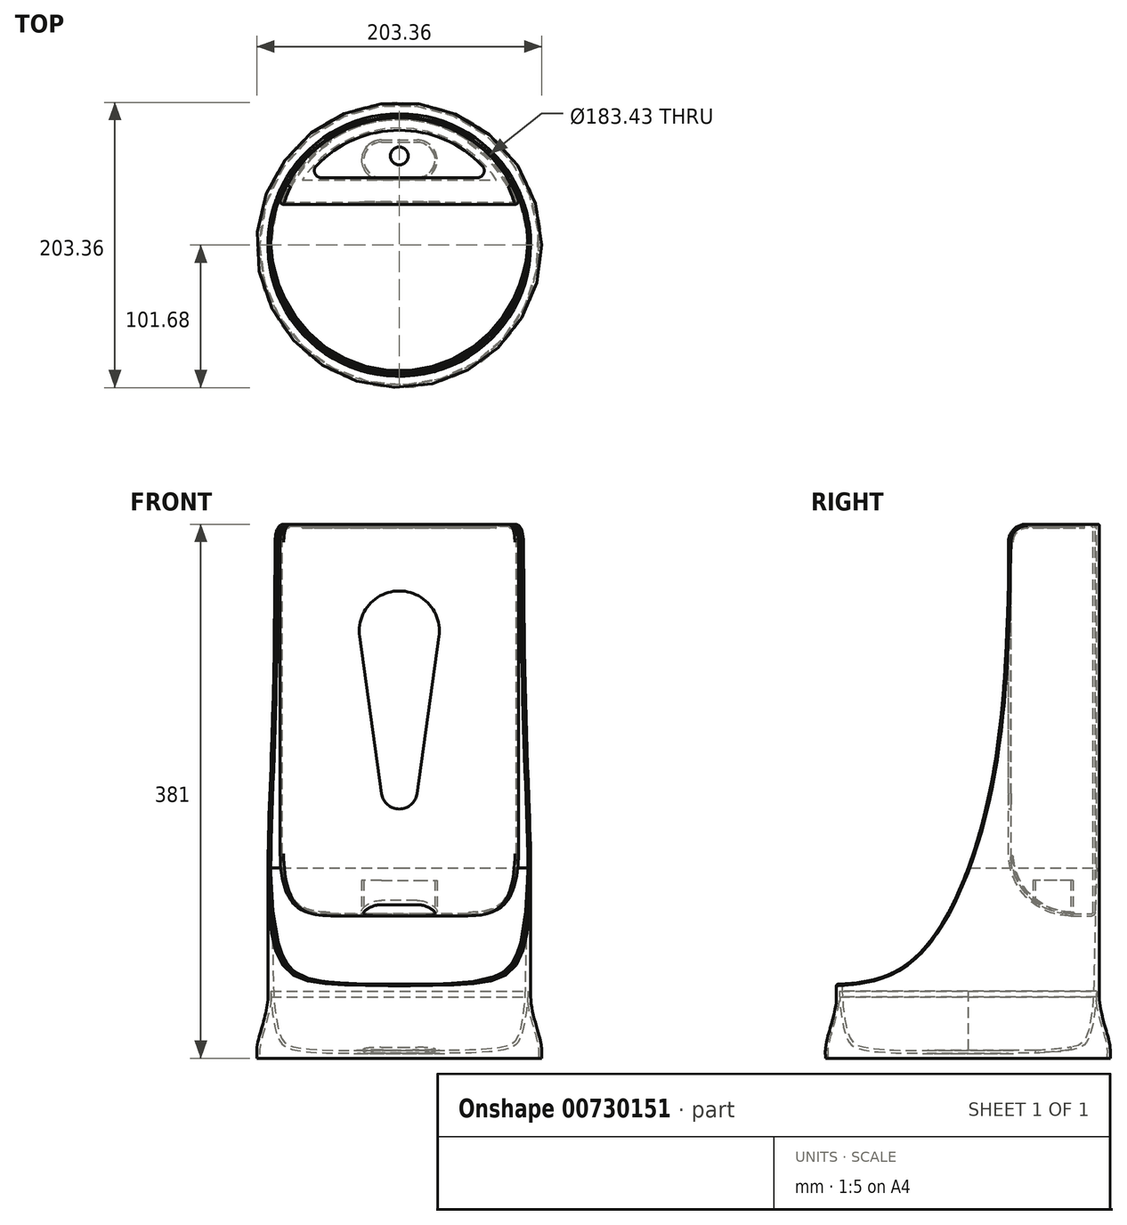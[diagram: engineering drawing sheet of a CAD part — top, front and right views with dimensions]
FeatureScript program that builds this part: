
annotation { "Feature Type Name" : "Feature", "Feature Type Description" : "" }
export const myFeature = defineFeature(function(context is Context, id is Id, definition is map)
    precondition{}
    {
        {
            var Q0;
            Q0=qCreatedBy(makeId("Right.planeOp"),FACE);
            var sketch = newSketch(context, id + "F0", { "sketchPlane" : qUnion([Q0])});
            skLineSegment(sketch, "E0", {"start": v(0, 343.86) * mm, "end": v(0, -187.02) * mm, "construction": true});
            skLineSegment(sketch, "E1", {"start": v(0, 381) * mm, "end": v(0, 0) * mm});
            skLineSegment(sketch, "E2", {"start": v(0, 0) * mm, "end": v(101.6, 0) * mm});
            skLineSegment(sketch, "E3", {"start": v(93.75, 381) * mm, "end": v(0, 381) * mm});
            skLineSegment(sketch, "E4", {"start": v(93.75, 381) * mm, "end": v(93.75, 43.78) * mm});
            skFitSpline(sketch, "E5", {"points": [v(93.75, 43.78) * mm, v(99.9, 15.52) * mm, v(101.6, 6.52) * mm, v(101.6, 0) * mm], "startDerivative": vector(0, -53.97) * mm, "endDerivative": vector(-0.88, -40.06) * mm});
            skSolve(sketch);
        }
        {
            var Q0;
            Q0=makeQuery(id+"F0.imprint","IMPRINT",FACE,{"disambiguationData":[TD([[makeQuery(id+"F0.imprint","IMPRINT",EDGE,{"derivedFrom":sQuery(id+"F0.wireOp",EDGE,"E1")}),1.0]])]});
            var Q1;
            Q1=sQuery(id+"F0.wireOp",EDGE,"E0");
            revolve(context, id + "F1", {"surfaceOperationType" : NewSurfaceOperationType.NEW, "entities" : qUnion([Q0]), "axis" : qUnion([Q1]), "revolveType" : RevolveType.FULL});
        }
        {
            var Q0;
            Q0=qCreatedBy(makeId("Right.planeOp"),FACE);
            var sketch = newSketch(context, id + "F2", { "sketchPlane" : qUnion([Q0])});
            skFitSpline(sketch, "E6.0", {"points": [v(93.75, 43.78) * mm, v(93.75, 34.95) * mm, v(100.28, 16.1) * mm, v(101.8, 6.5) * mm, v(101.67, 3.11) * mm, v(101.6, 0) * mm], "construction": true});
            skLineSegment(sketch, "E7.0", {"start": v(93.75, 381) * mm, "end": v(93.75, 43.78) * mm, "construction": true});
            skFitSpline(sketch, "E8.0", {"points": [v(91.72, 43.78) * mm, v(91.72, 41.36) * mm, v(92.29, 36.24) * mm, v(93.83, 29.57) * mm, v(95.23, 24.44) * mm, v(96.29, 20.8) * mm, v(97.1, 18) * mm, v(97.68, 15.97) * mm, v(98.06, 14.57) * mm, v(98.4, 13.29) * mm, v(98.77, 11.72) * mm, v(99.12, 10) * mm, v(99.4, 8.25) * mm, v(99.53, 7) * mm, v(99.6, 6.06) * mm, v(99.64, 5.16) * mm, v(99.65, 4) * mm, v(99.62, 2.33) * mm, v(99.59, 0.88) * mm, v(99.57, 0.04) * mm]});
            skLineSegment(sketch, "E8.1", {"start": v(91.72, 304.8) * mm, "end": v(91.72, 43.78) * mm, "construction": true});
            skLineSegment(sketch, "E9", {"start": v(91.72, 43.78) * mm, "end": v(91.72, 47.88) * mm});
            skFitSpline(sketch, "E10", {"points": [v(91.72, 47.88) * mm, v(86.67, 15.25) * mm, v(74.28, 5.84) * mm, v(29.74, 3.52) * mm], "startDerivative": vector(-1.81, -78.5) * mm, "endDerivative": vector(-58.98, 0) * mm});
            skLineSegment(sketch, "E11", {"start": v(29.74, 3.52) * mm, "end": v(0, 3.52) * mm});
            skLineSegment(sketch, "E12", {"start": v(0, 3.52) * mm, "end": v(0, -5.27) * mm});
            skLineSegment(sketch, "E13", {"start": v(0, -5.27) * mm, "end": v(98.97, -5.27) * mm});
            skLineSegment(sketch, "E14", {"start": v(98.97, -5.27) * mm, "end": v(99.57, 0.04) * mm});
            skSolve(sketch);
        }
        {
            var Q0;
            Q0 = qSketchRegion(id + "F2", true);
            var Q1;
            Q1=sQuery(id+"F0.wireOp",EDGE,"E0");
            revolve(context, id + "F3", {"operationType" : NewBodyOperationType.REMOVE, "surfaceOperationType" : NewSurfaceOperationType.NEW, "entities" : qUnion([Q0]), "axis" : qUnion([Q1]), "revolveType" : RevolveType.FULL, "oppositeDirection" : true});
        }
        {
            var Q0;
            Q0=makeQuery(id+"F1.opRevolve","SWEPT_FACE",FACE,{"disambiguationData":[OSD([sQuery(id+"F0.wireOp",EDGE,"E3")])]});
            shell(context, id + "F4", {"entities" : qUnion([Q0]), "thickness" : 2.03 * mm});
        }
        {
            var Q0;
            Q0=qCreatedBy(makeId("Right.planeOp"),FACE);
            var sketch = newSketch(context, id + "F5", { "sketchPlane" : qUnion([Q0])});
            skFitSpline(sketch, "E15", {"points": [v(29.87, 383.03) * mm, v(18.53, 206.1) * mm, v(-39.75, 69.98) * mm, v(-93.97, 52.7) * mm, v(-140.33, 52.7) * mm], "startDerivative": vector(-12.72, -336.18) * mm, "endDerivative": vector(-243.15, 2.79) * mm});
            skLineSegment(sketch, "E16", {"start": v(29.87, 383.03) * mm, "end": v(-142.32, 383.03) * mm});
            skLineSegment(sketch, "E17", {"start": v(-142.32, 383.03) * mm, "end": v(-140.33, 52.7) * mm});
            skSolve(sketch);
        }
        {
            var Q0;
            Q0=makeQuery(id+"F5.imprint","IMPRINT",FACE,{"disambiguationData":[TD([[makeQuery(id+"F5.imprint","IMPRINT",EDGE,{"derivedFrom":sQuery(id+"F5.wireOp",EDGE,"E15")}),-1.0]])]});
            extrude(context, id + "F6", {"entities" : qUnion([Q0]), "operationType" : NewBodyOperationType.REMOVE, "endBound" : BoundingType.THROUGH_ALL, "oppositeDirection" : true, "depth" : 25.4 * mm, "offsetDistance" : 25.4 * mm, "hasSecondDirection" : true, "secondDirectionBound" : BoundingType.THROUGH_ALL, "secondDirectionOppositeDirection" : false, "secondDirectionDepth" : 25.4 * mm});
        }
        {
            var Q0;
            Q0=makeQuery(id+"F6.boolean.opBoolean","INTERSECT",EDGE,{"disambiguationData":[OD(0.0)],"derivedFrom":[makeQuery(id+"F1.opRevolve","SWEPT_FACE",FACE,{"disambiguationData":[OSD([sQuery(id+"F0.wireOp",EDGE,"E3")])]}),makeQuery(id+"F6.opExtrude","SWEPT_FACE",FACE,{"disambiguationData":[OSD([sQuery(id+"F5.wireOp",EDGE,"E15")])]})]});
            var Q1;
            Q1=makeQuery(id+"F6.boolean.opBoolean","INTERSECT",EDGE,{"disambiguationData":[OD(1.0)],"derivedFrom":[makeQuery(id+"F1.opRevolve","SWEPT_FACE",FACE,{"disambiguationData":[OSD([sQuery(id+"F0.wireOp",EDGE,"E3")])]}),makeQuery(id+"F6.opExtrude","SWEPT_FACE",FACE,{"disambiguationData":[OSD([sQuery(id+"F5.wireOp",EDGE,"E15")])]})]});
            fillet(context, id + "F7", {"entities" : qUnion([Q0, Q1]), "radius" : 12.7 * mm, "tangentPropagation" : true, "allowEdgeOverflow" : false});
        }
        {
            var Q0;
            Q0=makeQuery(id+"F7.opFillet","BLEND_EDGE",EDGE,{"blendedFrom":[makeQuery(id+"F6.boolean.opBoolean","INTERSECT",EDGE,{"disambiguationData":[OD(0.0)],"derivedFrom":[makeQuery(id+"F1.opRevolve","SWEPT_FACE",FACE,{"disambiguationData":[OSD([sQuery(id+"F0.wireOp",EDGE,"E3")])]}),makeQuery(id+"F6.opExtrude","SWEPT_FACE",FACE,{"disambiguationData":[OSD([sQuery(id+"F5.wireOp",EDGE,"E15")])]})]}),makeQuery(id+"F4.opShell","OFFSET_FACE",FACE,{"disambiguationData":[OSD([sQuery(id+"F0.wireOp",EDGE,"E4")])]})],"blendedInto":[makeQuery(id+"F4.opShell","OFFSET_FACE",FACE,{"disambiguationData":[OSD([sQuery(id+"F0.wireOp",EDGE,"E4")])]})]});
            var Q1;
            Q1=makeQuery(id+"F7.opFillet","BLEND_EDGE",EDGE,{"blendedFrom":[makeQuery(id+"F6.boolean.opBoolean","INTERSECT",EDGE,{"disambiguationData":[OD(0.0)],"derivedFrom":[makeQuery(id+"F1.opRevolve","SWEPT_FACE",FACE,{"disambiguationData":[OSD([sQuery(id+"F0.wireOp",EDGE,"E3")])]}),makeQuery(id+"F6.opExtrude","SWEPT_FACE",FACE,{"disambiguationData":[OSD([sQuery(id+"F5.wireOp",EDGE,"E15")])]})]}),makeQuery(id+"F1.opRevolve","SWEPT_FACE",FACE,{"disambiguationData":[OSD([sQuery(id+"F0.wireOp",EDGE,"E4")])]})],"blendedInto":[makeQuery(id+"F1.opRevolve","SWEPT_FACE",FACE,{"disambiguationData":[OSD([sQuery(id+"F0.wireOp",EDGE,"E4")])]})]});
            var Q2;
            Q2=makeQuery(id+"F6.boolean.opBoolean","INTERSECT",EDGE,{"disambiguationData":[OD(0.0)],"derivedFrom":[makeQuery(id+"F4.opShell","OFFSET_FACE",FACE,{"disambiguationData":[OSD([sQuery(id+"F0.wireOp",EDGE,"E4")])]}),makeQuery(id+"F6.opExtrude","SWEPT_FACE",FACE,{"disambiguationData":[OSD([sQuery(id+"F5.wireOp",EDGE,"E15")])]})]});
            var Q3;
            Q3=makeQuery(id+"F6.boolean.opBoolean","INTERSECT",EDGE,{"derivedFrom":[makeQuery(id+"F4.opShell","OFFSET_FACE",FACE,{"disambiguationData":[OSD([sQuery(id+"F2.wireOp",EDGE,"E10")])]}),makeQuery(id+"F6.opExtrude","SWEPT_FACE",FACE,{"disambiguationData":[OSD([sQuery(id+"F5.wireOp",EDGE,"E15")])]})]});
            fillet(context, id + "F8", {"entities" : qUnion([Q0, Q1, Q2, Q3]), "radius" : 1.02 * mm, "tangentPropagation" : true, "allowEdgeOverflow" : false});
        }
        {
            var Q0;
            Q0=qCreatedBy(makeId("Top.planeOp"),FACE);
            var Q1;
            {var subQ0=sQuery(id+"F0.wireOp",EDGE,"E4");var subQ1=sQuery(id+"F0.wireOp",EDGE,"E3");var subQ2=makeQuery(id+"F6.boolean.opBoolean","INTERSECT",EDGE,{"disambiguationData":[OD(1.0)],"derivedFrom":[makeQuery(id+"F1.opRevolve","SWEPT_FACE",FACE,{"disambiguationData":[OSD([subQ1])]}),makeQuery(id+"F6.opExtrude","SWEPT_FACE",FACE,{"disambiguationData":[OSD([sQuery(id+"F5.wireOp",EDGE,"E15")])]})]});Q1=makeQuery(id+"F8.opFillet","BLEND_VERTEX",VERTEX,{"blendedFrom":[makeQuery(id+"F1.opRevolve","SWEPT_EDGE",EDGE,{"disambiguationData":[OSD([subQ1,subQ0])]}),makeQuery(id+"F4.opShell","OFFSET_EDGE",EDGE,{"disambiguationData":[OSD([subQ1,subQ0])]}),makeQuery(id+"F7.opFillet","BLEND_EDGE",EDGE,{"blendedFrom":[subQ2,makeQuery(id+"F1.opRevolve","SWEPT_FACE",FACE,{"disambiguationData":[OSD([subQ0])]})],"blendedInto":[makeQuery(id+"F1.opRevolve","SWEPT_FACE",FACE,{"disambiguationData":[OSD([subQ0])]})]}),makeQuery(id+"F7.opFillet","BLEND_EDGE",EDGE,{"blendedFrom":[subQ2,makeQuery(id+"F4.opShell","OFFSET_FACE",FACE,{"disambiguationData":[OSD([subQ0])]})],"blendedInto":[makeQuery(id+"F4.opShell","OFFSET_FACE",FACE,{"disambiguationData":[OSD([subQ0])]})]})],"blendedInto":[]});}
            cPlane(context, id + "F9", {"entities" : qUnion([Q0, Q1]), "cplaneType" : CPlaneType.PLANE_POINT, "offset" : 25.4 * mm, "width" : 152.4 * mm, "height" : 152.4 * mm});
        }
        {
            var Q0;
            Q0=qCreatedBy(id+"F9.planeOp",FACE);
            var sketch = newSketch(context, id + "F10", { "sketchPlane" : qUnion([Q0])});
            skArc(sketch, "E18", {"start": v(86.06, 28.98) * mm, "mid": v(0, 90.8) * mm, "end": v(-86.06, 28.98) * mm});
            skLineSegment(sketch, "E19", {"start": v(-86.06, 28.98) * mm, "end": v(86.06, 28.98) * mm});
            skSolve(sketch);
        }
        {
            var Q0;
            Q0=makeQuery(id+"F10.imprint","IMPRINT",FACE,{"disambiguationData":[TD([[makeQuery(id+"F10.imprint","IMPRINT",EDGE,{"derivedFrom":sQuery(id+"F10.wireOp",EDGE,"E18")}),1.0]])]});
            extrude(context, id + "F11", {"entities" : qUnion([Q0]), "oppositeDirection" : true, "depth" : 279.4 * mm, "offsetDistance" : 25.4 * mm});
        }
        {
            var Q0;
            Q0=makeQuery(id+"F11.opExtrude","CAP_EDGE",EDGE,{"disambiguationData":[OSD([sQuery(id+"F10.wireOp",EDGE,"E19")])],"isStart":false});
            fillet(context, id + "F12", {"entities" : qUnion([Q0]), "radius" : 44.45 * mm, "tangentPropagation" : true, "allowEdgeOverflow" : false});
        }
        {
            var Q0;
            Q0=makeQuery(id+"F11.opExtrude","CAP_EDGE",EDGE,{"disambiguationData":[OSD([sQuery(id+"F10.wireOp",EDGE,"E19")])],"isStart":true});
            fillet(context, id + "F13", {"entities" : qUnion([Q0]), "radius" : 12.7 * mm, "tangentPropagation" : true, "allowEdgeOverflow" : false});
        }
        {
            var Q0;
            {var subQ0=sQuery(id+"F10.wireOp",EDGE,"E19");var subQ1=sQuery(id+"F10.wireOp",EDGE,"E18");Q0=makeQuery(id+"F11.opExtrude","SWEPT_EDGE",EDGE,{"disambiguationData":[OSD([subQ1,subQ0]),TDD([makeQuery(id+"F10.imprint","INTERSECT",VERTEX,{"disambiguationData":[OD(1.0)],"derivedFrom":[subQ1,subQ0]})])]});}
            fillet(context, id + "F14", {"entities" : qUnion([Q0]), "radius" : 2.54 * mm, "tangentPropagation" : true, "allowEdgeOverflow" : false});
        }
        {
            var Q0;
            Q0=makeQuery(id+"F11.opExtrude","CAP_FACE",FACE,{"disambiguationData":[OSD([sQuery(id+"F10.wireOp",EDGE,"E18"),sQuery(id+"F10.wireOp",EDGE,"E19")])],"isStart":true});
            var sketch = newSketch(context, id + "F15", { "sketchPlane" : qUnion([Q0])});
            skArc(sketch, "E20.0", {"start": v(66.36, 48.03) * mm, "mid": v(0, 81.91) * mm, "end": v(-66.36, 48.03) * mm});
            skLineSegment(sketch, "E20.1", {"start": v(-66.36, 48.03) * mm, "end": v(66.36, 48.03) * mm});
            skSolve(sketch);
        }
        {
            var Q0;
            Q0 = qSketchRegion(id + "F15", true);
            extrude(context, id + "F16", {"entities" : qUnion([Q0]), "operationType" : NewBodyOperationType.REMOVE, "oppositeDirection" : true, "depth" : 2.54 * mm, "offsetDistance" : 25.4 * mm});
        }
        {
            var Q0;
            Q0=qCreatedBy(makeId("Top.planeOp"),FACE);
            var sketch = newSketch(context, id + "F17", { "sketchPlane" : qUnion([Q0])});
            skArc(sketch, "E21", {"start": v(-12.7, 73.43) * mm, "mid": v(-25.4, 60.73) * mm, "end": v(-12.7, 48.03) * mm});
            skArc(sketch, "E22", {"start": v(12.7, 48.03) * mm, "mid": v(25.4, 60.73) * mm, "end": v(12.7, 73.43) * mm});
            skLineSegment(sketch, "E23", {"start": v(-12.7, 48.03) * mm, "end": v(12.7, 48.03) * mm});
            skLineSegment(sketch, "E24", {"start": v(12.7, 73.43) * mm, "end": v(-12.7, 73.43) * mm});
            skSolve(sketch);
        }
        {
            var Q0;
            Q0=makeQuery(id+"F17.imprint","IMPRINT",FACE,{"disambiguationData":[TD([[makeQuery(id+"F17.imprint","IMPRINT",EDGE,{"derivedFrom":sQuery(id+"F17.wireOp",EDGE,"E21")}),1.0]])]});
            extrude(context, id + "F18", {"entities" : qUnion([Q0]), "operationType" : NewBodyOperationType.REMOVE, "depth" : 127 * mm, "offsetDistance" : 25.4 * mm});
        }
        {
            var Q0;
            Q0=makeQuery(id+"F16.boolean.opBoolean","COPY",FACE,{"derivedFrom":makeQuery(id+"F16.opExtrude","CAP_FACE",FACE,{"disambiguationData":[OSD([sQuery(id+"F15.wireOp",EDGE,"E20.0"),sQuery(id+"F15.wireOp",EDGE,"E20.1")])],"isStart":false})});
            var Q1;
            Q1=makeQuery(id+"F18.boolean.opBoolean","COPY",FACE,{"derivedFrom":makeQuery(id+"F18.opExtrude","CAP_FACE",FACE,{"disambiguationData":[OSD([sQuery(id+"F17.wireOp",EDGE,"E21"),sQuery(id+"F17.wireOp",EDGE,"E22"),sQuery(id+"F17.wireOp",EDGE,"E23"),sQuery(id+"F17.wireOp",EDGE,"E24")])],"isStart":false})});
            shell(context, id + "F19", {"entities" : qUnion([Q0, Q1]), "thickness" : 1.52 * mm});
        }
        {
            var Q0;
            {var subQ0=sQuery(id+"F15.wireOp",EDGE,"E20.1");var subQ1=sQuery(id+"F15.wireOp",EDGE,"E20.0");Q0=makeQuery(id+"F16.boolean.opBoolean","COPY",EDGE,{"derivedFrom":makeQuery(id+"F16.opExtrude","SWEPT_EDGE",EDGE,{"disambiguationData":[OSD([subQ1,subQ0]),TDD([makeQuery(id+"F15.imprint","INTERSECT",VERTEX,{"disambiguationData":[OD(1.0)],"derivedFrom":[subQ1,subQ0]})])]})});}
            var Q1;
            {var subQ0=sQuery(id+"F15.wireOp",EDGE,"E20.1");var subQ1=sQuery(id+"F15.wireOp",EDGE,"E20.0");Q1=makeQuery(id+"F16.boolean.opBoolean","COPY",EDGE,{"derivedFrom":makeQuery(id+"F16.opExtrude","SWEPT_EDGE",EDGE,{"disambiguationData":[OSD([subQ1,subQ0]),TDD([makeQuery(id+"F15.imprint","INTERSECT",VERTEX,{"disambiguationData":[OD(0.0)],"derivedFrom":[subQ1,subQ0]})])]})});}
            fillet(context, id + "F20", {"entities" : qUnion([Q0, Q1]), "radius" : 5.08 * mm, "tangentPropagation" : true, "allowEdgeOverflow" : false});
        }
        {
            var Q0;
            Q0=qCreatedBy(makeId("Front.planeOp"),FACE);
            var sketch = newSketch(context, id + "F21", { "sketchPlane" : qUnion([Q0])});
            skArc(sketch, "E25", {"start": v(28.3, 300.83) * mm, "mid": v(0, 333.38) * mm, "end": v(-28.3, 300.83) * mm});
            skArc(sketch, "E26", {"start": v(-12.58, 188.74) * mm, "mid": v(0, 177.8) * mm, "end": v(12.58, 188.74) * mm});
            skLineSegment(sketch, "E27", {"start": v(-28.3, 300.83) * mm, "end": v(-12.58, 188.74) * mm});
            skLineSegment(sketch, "E28", {"start": v(12.58, 188.74) * mm, "end": v(28.3, 300.83) * mm});
            skSolve(sketch);
        }
        {
            var Q0;
            Q0=makeQuery(id+"F21.imprint","IMPRINT",FACE,{"disambiguationData":[TD([[makeQuery(id+"F21.imprint","IMPRINT",EDGE,{"derivedFrom":sQuery(id+"F21.wireOp",EDGE,"E25")}),1.0]])]});
            extrude(context, id + "F22", {"entities" : qUnion([Q0]), "operationType" : NewBodyOperationType.REMOVE, "oppositeDirection" : true, "depth" : 38.1 * mm, "offsetDistance" : 25.4 * mm});
        }
        {
            var Q0;
            Q0=makeQuery(id+"F11.opExtrude","SWEPT_FACE",FACE,{"disambiguationData":[OSD([sQuery(id+"F10.wireOp",EDGE,"E19")])]});
            var sketch = newSketch(context, id + "F23", { "sketchPlane" : qUnion([Q0])});
            skArc(sketch, "E29.0", {"start": v(28.3, 300.83) * mm, "mid": v(0, 333.38) * mm, "end": v(-28.3, 300.83) * mm});
            skLineSegment(sketch, "E30.0", {"start": v(-28.3, 300.83) * mm, "end": v(-12.58, 188.74) * mm});
            skLineSegment(sketch, "E31.0", {"start": v(12.58, 188.74) * mm, "end": v(28.3, 300.83) * mm});
            skArc(sketch, "E32.0", {"start": v(-12.58, 188.74) * mm, "mid": v(0, 177.8) * mm, "end": v(12.58, 188.74) * mm});
            skSolve(sketch);
        }
        {
            var Q0;
            Q0 = qSketchRegion(id + "F23", true);
            extrude(context, id + "F24", {"entities" : qUnion([Q0]), "oppositeDirection" : true, "depth" : 2.03 * mm, "offsetDistance" : 25.4 * mm});
        }
        {
            var Q0;
            Q0=makeQuery(id+"F11.opExtrude","CAP_FACE",FACE,{"disambiguationData":[OSD([sQuery(id+"F10.wireOp",EDGE,"E18"),sQuery(id+"F10.wireOp",EDGE,"E19")])],"isStart":true});
            var sketch = newSketch(context, id + "F25", { "sketchPlane" : qUnion([Q0])});
            skArc(sketch, "E33.0", {"start": v(59.2, 56.62) * mm, "mid": v(0, 81.91) * mm, "end": v(-59.2, 56.62) * mm});
            skArc(sketch, "E34.0", {"start": v(-55.52, 48.03) * mm, "mid": v(-60.2, 51.12) * mm, "end": v(-59.2, 56.62) * mm});
            skLineSegment(sketch, "E35.0", {"start": v(-55.52, 48.03) * mm, "end": v(55.52, 48.03) * mm});
            skArc(sketch, "E36.0", {"start": v(59.2, 56.62) * mm, "mid": v(60.2, 51.12) * mm, "end": v(55.52, 48.03) * mm});
            skCircle(sketch, "E37", {"center": v(0, 63.6) * mm, "radius": 6.35 * mm});
            skSolve(sketch);
        }
        {
            var Q0;
            Q0 = qSketchRegion(id + "F25", true);
            extrude(context, id + "F26", {"entities" : qUnion([Q0]), "oppositeDirection" : true, "depth" : 2.03 * mm, "offsetDistance" : 25.4 * mm});
        }
    });
